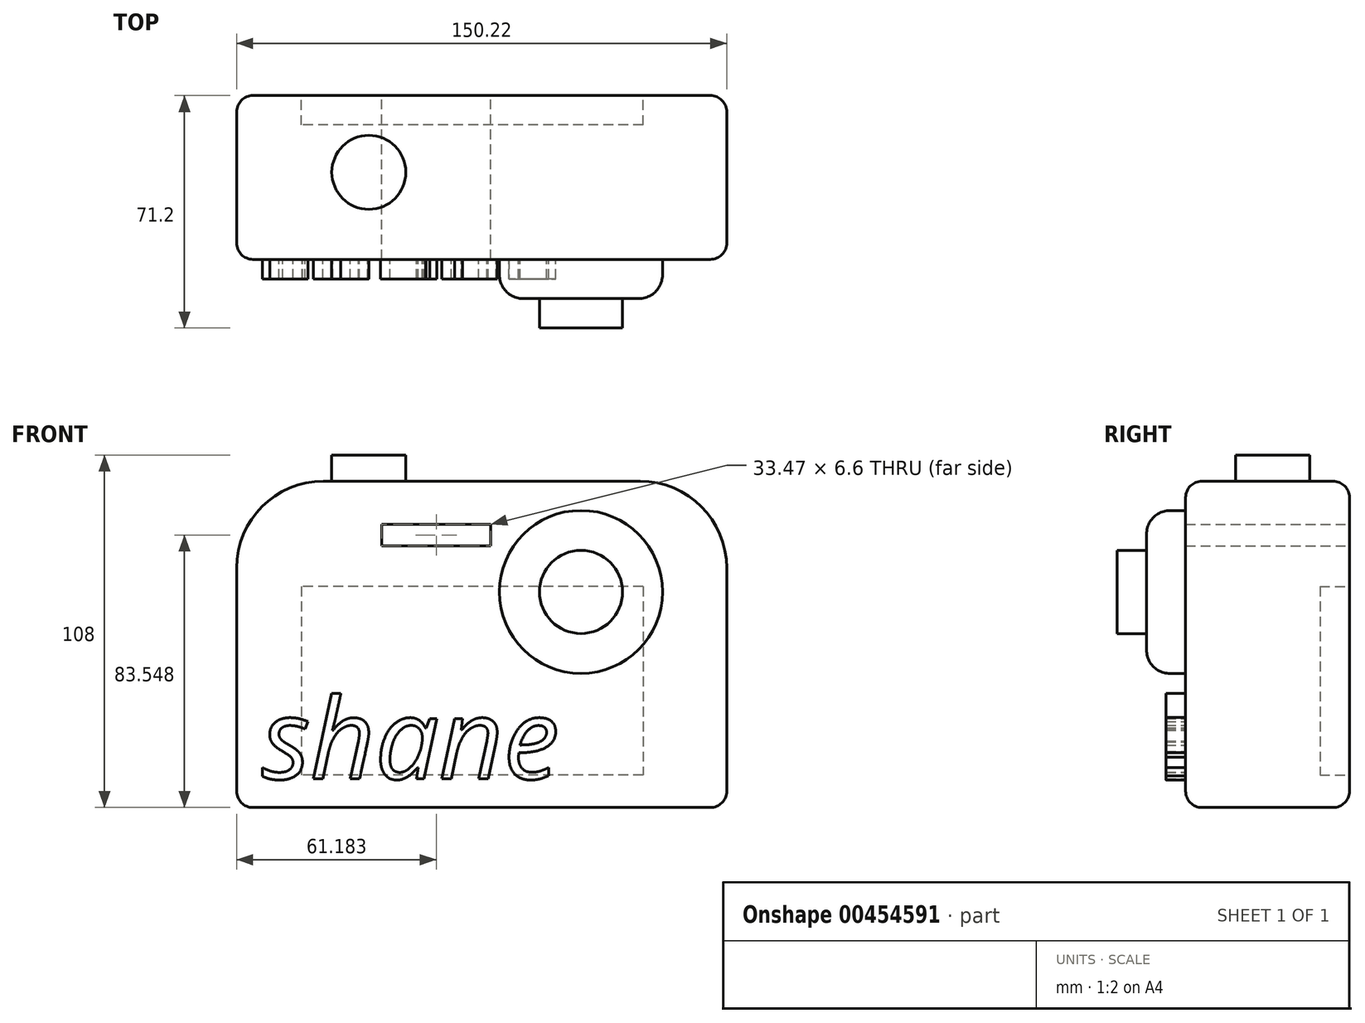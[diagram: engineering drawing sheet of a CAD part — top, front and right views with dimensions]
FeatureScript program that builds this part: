
annotation { "Feature Type Name" : "Feature", "Feature Type Description" : "" }
export const myFeature = defineFeature(function(context is Context, id is Id, definition is map)
    precondition{}
    {
        {
            var Q0;
            Q0=qCreatedBy(makeId("Top.planeOp"),FACE);
            var sketch = newSketch(context, id + "F0", { "sketchPlane" : qUnion([Q0])});
            skLineSegment(sketch, "E0.bottom", {"start": v(-69.23, 27.25) * mm, "end": v(80.99, 27.25) * mm});
            skLineSegment(sketch, "E0.top", {"start": v(-69.23, -22.95) * mm, "end": v(80.99, -22.95) * mm});
            skLineSegment(sketch, "E0.left", {"start": v(-69.23, 27.25) * mm, "end": v(-69.23, -22.95) * mm});
            skLineSegment(sketch, "E0.right", {"start": v(80.99, 27.25) * mm, "end": v(80.99, -22.95) * mm});
            skSolve(sketch);
        }
        {
            var Q0;
            Q0 = qSketchRegion(id + "F0", true);
            extrude(context, id + "F1", {"entities" : qUnion([Q0]), "depth" : 100 * mm});
        }
        {
            var Q0;
            Q0=makeQuery(id+"F1.opExtrude","CAP_EDGE",EDGE,{"disambiguationData":[OSD([sQuery(id+"F0.wireOp",EDGE,"E0.right")])],"isStart":false});
            var Q1;
            Q1=makeQuery(id+"F1.opExtrude","CAP_EDGE",EDGE,{"disambiguationData":[OSD([sQuery(id+"F0.wireOp",EDGE,"E0.left")])],"isStart":false});
            fillet(context, id + "F2", {"entities" : qUnion([Q0, Q1]), "radius" : 26.56 * mm, "tangentPropagation" : true, "allowEdgeOverflow" : false});
        }
        {
            var Q0;
            Q0=makeQuery(id+"F1.opExtrude","CAP_EDGE",EDGE,{"disambiguationData":[OSD([sQuery(id+"F0.wireOp",EDGE,"E0.left")])],"isStart":true});
            var Q1;
            Q1=makeQuery(id+"F1.opExtrude","CAP_EDGE",EDGE,{"disambiguationData":[OSD([sQuery(id+"F0.wireOp",EDGE,"E0.right")])],"isStart":true});
            var Q2;
            Q2=makeQuery(id+"F1.opExtrude","CAP_EDGE",EDGE,{"disambiguationData":[OSD([sQuery(id+"F0.wireOp",EDGE,"E0.top")])],"isStart":true});
            var Q3;
            Q3=makeQuery(id+"F1.opExtrude","CAP_EDGE",EDGE,{"disambiguationData":[OSD([sQuery(id+"F0.wireOp",EDGE,"E0.bottom")])],"isStart":true});
            var Q4;
            Q4=makeQuery(id+"F1.opExtrude","SWEPT_EDGE",EDGE,{"disambiguationData":[OSD([sQuery(id+"F0.wireOp",EDGE,"E0.top"),sQuery(id+"F0.wireOp",EDGE,"E0.left")])]});
            var Q5;
            Q5=makeQuery(id+"F1.opExtrude","SWEPT_EDGE",EDGE,{"disambiguationData":[OSD([sQuery(id+"F0.wireOp",EDGE,"E0.bottom"),sQuery(id+"F0.wireOp",EDGE,"E0.left")])]});
            fillet(context, id + "F3", {"entities" : qUnion([Q0, Q1, Q2, Q3, Q4, Q5]), "radius" : 5 * mm, "tangentPropagation" : true, "allowEdgeOverflow" : false});
        }
        {
            var Q0;
            Q0=makeQuery(id+"F1.opExtrude","SWEPT_FACE",FACE,{"disambiguationData":[OSD([sQuery(id+"F0.wireOp",EDGE,"E0.top")])]});
            var sketch = newSketch(context, id + "F4", { "sketchPlane" : qUnion([Q0])});
            skCircle(sketch, "E1", {"center": v(36.3, 66.06) * mm, "radius": 24.99 * mm});
            skSolve(sketch);
        }
        {
            var Q0;
            Q0=makeQuery(id+"F4.imprint","IMPRINT",FACE,{"disambiguationData":[TD([[makeQuery(id+"F4.imprint","IMPRINT",EDGE,{"derivedFrom":sQuery(id+"F4.wireOp",EDGE,"E1")}),1.0]])]});
            extrude(context, id + "F5", {"entities" : qUnion([Q0]), "operationType" : NewBodyOperationType.ADD, "depth" : 12 * mm});
        }
        {
            var Q0;
            Q0=makeQuery(id+"F1.opExtrude","CAP_FACE",FACE,{"disambiguationData":[OSD([sQuery(id+"F0.wireOp",EDGE,"E0.bottom"),sQuery(id+"F0.wireOp",EDGE,"E0.top"),sQuery(id+"F0.wireOp",EDGE,"E0.left"),sQuery(id+"F0.wireOp",EDGE,"E0.right")])],"isStart":false});
            var sketch = newSketch(context, id + "F6", { "sketchPlane" : qUnion([Q0])});
            skCircle(sketch, "E2", {"center": v(-28.73, 3.73) * mm, "radius": 11.35 * mm});
            skSolve(sketch);
        }
        {
            var Q0;
            Q0=makeQuery(id+"F6.imprint","IMPRINT",FACE,{"disambiguationData":[TD([[makeQuery(id+"F6.imprint","IMPRINT",EDGE,{"derivedFrom":sQuery(id+"F6.wireOp",EDGE,"E2")}),1.0]])]});
            extrude(context, id + "F7", {"entities" : qUnion([Q0]), "operationType" : NewBodyOperationType.ADD, "depth" : 8 * mm});
        }
        {
            var Q0;
            Q0=makeQuery(id+"F5.opExtrude","CAP_FACE",FACE,{"disambiguationData":[OSD([sQuery(id+"F4.wireOp",EDGE,"E1")])],"isStart":false});
            fillet(context, id + "F8", {"entities" : qUnion([Q0]), "radius" : 7.24 * mm, "tangentPropagation" : true, "allowEdgeOverflow" : false});
        }
        {
            var Q0;
            Q0=makeQuery(id+"F1.opExtrude","SWEPT_FACE",FACE,{"disambiguationData":[OSD([sQuery(id+"F0.wireOp",EDGE,"E0.top")])]});
            var sketch = newSketch(context, id + "F9", { "sketchPlane" : qUnion([Q0])});
            skText(sketch, "E3", { "text": "shane", "fontName": "OpenSans-Italic.ttf"});
            const initialGuessF9  = {"E3": [-0.06143, 0.00876, 1, 0, 0.02482]};
            skSetInitialGuess(sketch, initialGuessF9);
            skSolve(sketch);
        }
        {
            var Q0;
            Q0 = qSketchRegion(id + "F9", true);
            extrude(context, id + "F10", {"entities" : qUnion([Q0]), "operationType" : NewBodyOperationType.ADD, "depth" : 6 * mm});
        }
        {
            var Q0;
            Q0=makeQuery(id+"F1.opExtrude","SWEPT_FACE",FACE,{"disambiguationData":[OSD([sQuery(id+"F0.wireOp",EDGE,"E0.bottom")])]});
            var sketch = newSketch(context, id + "F11", { "sketchPlane" : qUnion([Q0])});
            skLineSegment(sketch, "E4.bottom", {"start": v(-8.69, 86.85) * mm, "end": v(24.78, 86.85) * mm});
            skLineSegment(sketch, "E4.top", {"start": v(-8.69, 80.25) * mm, "end": v(24.78, 80.25) * mm});
            skLineSegment(sketch, "E4.left", {"start": v(-8.69, 86.85) * mm, "end": v(-8.69, 80.25) * mm});
            skLineSegment(sketch, "E4.right", {"start": v(24.78, 86.85) * mm, "end": v(24.78, 80.25) * mm});
            skSolve(sketch);
        }
        {
            var Q0;
            Q0=makeQuery(id+"F11.imprint","IMPRINT",FACE,{"disambiguationData":[TD([[makeQuery(id+"F11.imprint","IMPRINT",EDGE,{"derivedFrom":sQuery(id+"F11.wireOp",EDGE,"E4.bottom")}),-1.0]])]});
            extrude(context, id + "F12", {"entities" : qUnion([Q0]), "operationType" : NewBodyOperationType.REMOVE, "oppositeDirection" : true, "depth" : 51 * mm});
        }
        {
            var Q0;
            Q0=makeQuery(id+"F1.opExtrude","SWEPT_FACE",FACE,{"disambiguationData":[OSD([sQuery(id+"F0.wireOp",EDGE,"E0.bottom")])]});
            var sketch = newSketch(context, id + "F13", { "sketchPlane" : qUnion([Q0])});
            skLineSegment(sketch, "E5.bottom", {"start": v(-55.36, 67.72) * mm, "end": v(49.37, 67.72) * mm});
            skLineSegment(sketch, "E5.top", {"start": v(-55.36, 9.9) * mm, "end": v(49.37, 9.9) * mm});
            skLineSegment(sketch, "E5.left", {"start": v(-55.36, 67.72) * mm, "end": v(-55.36, 9.9) * mm});
            skLineSegment(sketch, "E5.right", {"start": v(49.37, 67.72) * mm, "end": v(49.37, 9.9) * mm});
            skSolve(sketch);
        }
        {
            var Q0;
            Q0=makeQuery(id+"F13.imprint","IMPRINT",FACE,{"disambiguationData":[TD([[makeQuery(id+"F13.imprint","IMPRINT",EDGE,{"derivedFrom":sQuery(id+"F13.wireOp",EDGE,"E5.bottom")}),-1.0]])]});
            extrude(context, id + "F14", {"entities" : qUnion([Q0]), "operationType" : NewBodyOperationType.REMOVE, "oppositeDirection" : true, "depth" : 9 * mm});
        }
        {
            var Q0;
            Q0=makeQuery(id+"F5.opExtrude","CAP_FACE",FACE,{"disambiguationData":[OSD([sQuery(id+"F4.wireOp",EDGE,"E1")])],"isStart":false});
            var sketch = newSketch(context, id + "F15", { "sketchPlane" : qUnion([Q0])});
            skCircle(sketch, "E6", {"center": v(36.3, 66.06) * mm, "radius": 12.73 * mm});
            skSolve(sketch);
        }
        {
            var Q0;
            Q0=makeQuery(id+"F15.imprint","IMPRINT",FACE,{"disambiguationData":[TD([[makeQuery(id+"F15.imprint","IMPRINT",EDGE,{"derivedFrom":sQuery(id+"F15.wireOp",EDGE,"E6")}),1.0]])]});
            extrude(context, id + "F16", {"entities" : qUnion([Q0]), "operationType" : NewBodyOperationType.ADD, "depth" : 9 * mm});
        }
    });
